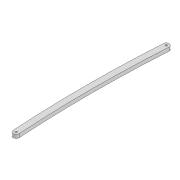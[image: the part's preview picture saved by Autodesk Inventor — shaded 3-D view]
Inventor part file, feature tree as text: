
AUTODESK INVENTOR PART (.ipt)
format: ipt  version: 2022 (Build 260153000, 153)  size: 93,696 bytes
history: native  units: mm
features: extrude x1, sketch x1
ambient origin geometry x8: Origin, YZ Plane, XZ Plane, XY Plane, X Axis, Y Axis, Z Axis, Center Point
bodies: Solid1 (feature_tree)
feature tree (2):
  extrude  "Extrusion1"  Depth=2000.0mm
  sketch  "Sketch1"  dims[d0=3.3mm d1=3.3mm d2=10.0mm d3=253.429mm d6=6.0mm d7=0.0mm d16=2000.0mm d17=2000.0mm]
